# Revit family: Hager-Volta-IP30-Surface_mounted-sistema-CH-it
name_source: partatom
category: Electrical Equipment
units: mm (PartAtom-declared; Revit-internal decimal feet)

## family parameters
Cut with Voids When Loaded = No
Host = Face
Panel Configuration = Two Columns, Circuits Across
Part Type = Panelboard
Room Calculation Point = No
Round Connector Dimension = Use Diameter
Shared = No

## types (6) — shared parameters
EF000003 - Tipo di montaggio = EV000384 - A parete
EF000008 - Larghezza = 305 mm  [stored 1.00066 ft]
EF000049 - profondità = 96 mm  [stored 0.314961 ft]
EF000116 - numero RAL = 9010
EF000118 - con piastra di montaggio = No
EF000339 - tipo di copertura = EV004216 - porta
EF001062 - esecuzione EMC = No
EF001088 - possibilità di applicazione = Yes
EF002950 - Numero moduli DIN = 12
EF004462 - tipo di chiusura = EV000154 - altri
EF005474 - grado di protezione (IP) = EV006410 - IP30
EF006244 - coperchio/porta trasparente = No
EF006306 - con serratura = No
EF009212 - esecuzione coperchio = EV009916 - con taglio
EF015776 - Morsettiera di terra = No
EF015777 - Morsettiera neutra = No
EF015941 - Segnale di passaggio porta = No
HG000001 - Numero di colonne = 1
HG000002 - Con porta = Yes
HG000003 - Gamma = Volta
HG000005 - Spessore = 3 mm  [stored 0.00984252 ft]
HG000006 - Ad incasso = No
HG000009 - Porta doppia a battente = No
HG000010 - Porte asimmetriche = No
HG000011 - File vuote nella parte basse = No
HG000017 - Distanza tra i poli = 18 mm  [stored 0.0590551 ft]
Manufacturer = Hager
Type Comments = Volta
zero-valued in all types: Default Elevation, EF000218 - profondità di incasso, EF000332 - Altezza della parte incassata, EF000846 - larghezza di montaggio, HG000007 - Numero di colonne vuote, HG000008 - Numero di file vuote

## per-type parameters (varying)
| type | EF000007 - colore | EF000040 - Altezza | EF000266 - numero di file | EF001131 - profondità interna | EF001134 - barra DIN | EF001596 - Attacco Lampada | HG000004 - Codice produttore | Model |
| A parete IP30 L305 A245 P96.5 12 Unità di divisione - VA12A |  | 245 mm | 1 | 0 mm  [stored 0 ft] | No |  | VA12A | VA12A |
| A parete IP30 L305 A370 P96.5 12 Unità di divisione - VA24A |  | 370 mm | 2 | 0 mm  [stored 0 ft] | No |  | VA24A | VA24A |
| A parete IP30 L305 A515 P96.5 12 Unità di divisione - VA36A |  | 515 mm | 3 | 0 mm  [stored 0 ft] | No |  | VA36A | VA36A |
| A parete IP30 L305 A515 P96.5 12 Unità di divisione - VA36RM | EV000202 - bianco | 515 mm | 3 | 92 mm | Yes | EV000139 - plastica | VA36RM | VA36RM |
| A parete IP30 L305 A640 P96.5 12 Unità di divisione - VA48A |  | 640 mm  [stored 2.09974 ft] | 4 | 0 mm  [stored 0 ft] | No |  | VA48A | VA48A |
| A parete IP30 L305 A640 P96.5 12 Unità di divisione - VA48RM | EV000202 - bianco | 640 mm  [stored 2.09974 ft] | 4 | 92 mm | Yes | EV000139 - plastica | VA48RM | VA48RM |

note: [stored X ft] marks values corroborated as IEEE doubles in the binary element streams (Revit-internal decimal feet)

## geometry (parser evidence)
native form markers: Sweep x17
no freeform markers — native parametric forms only
